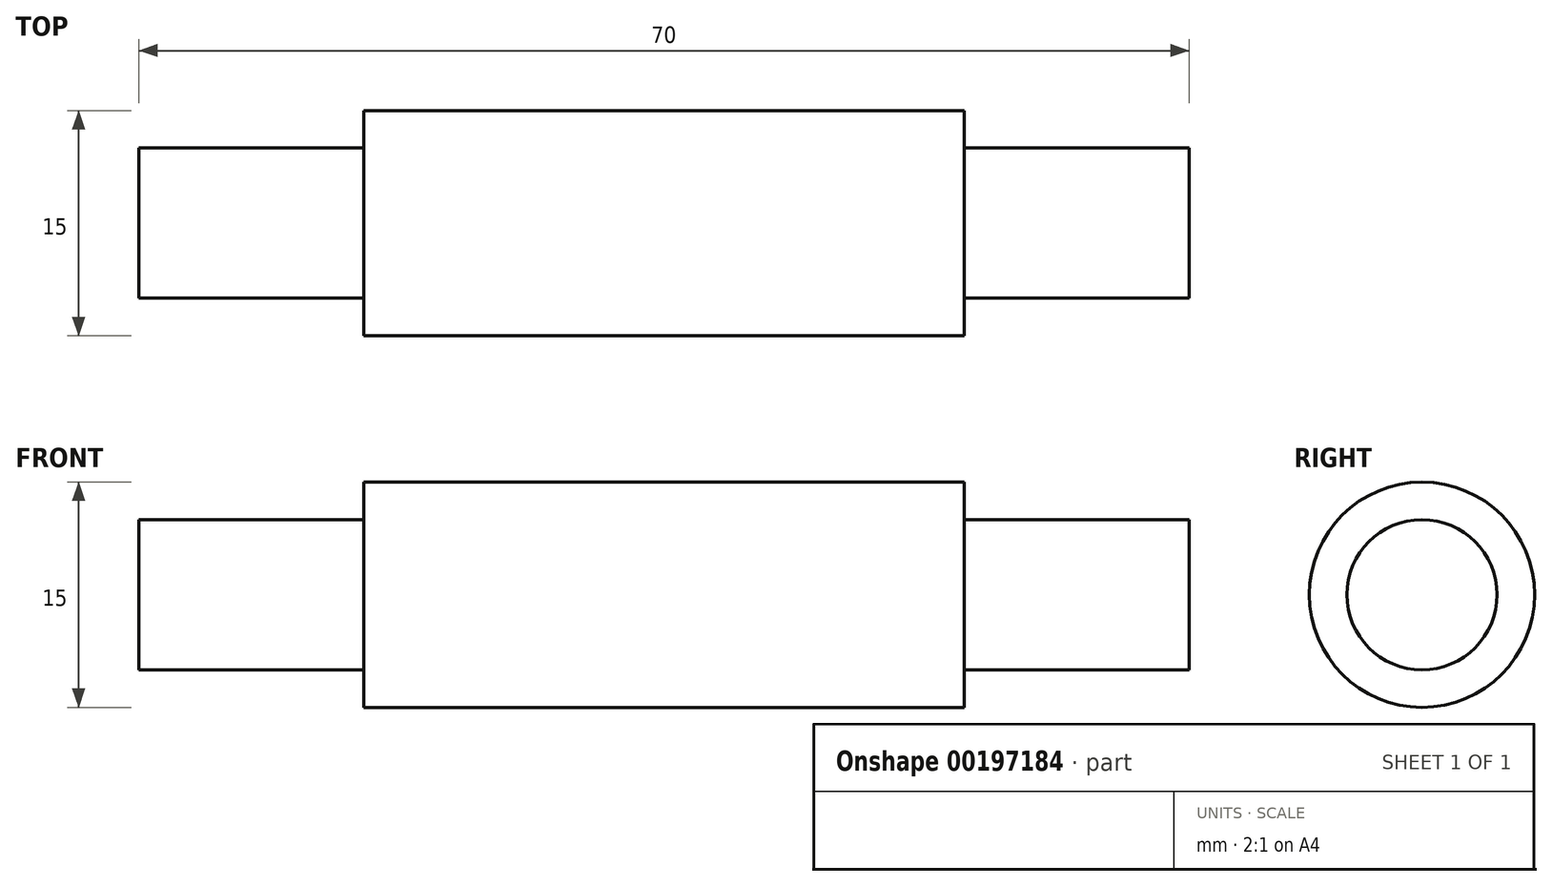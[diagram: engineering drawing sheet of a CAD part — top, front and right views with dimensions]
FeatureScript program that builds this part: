
annotation { "Feature Type Name" : "Feature", "Feature Type Description" : "" }
export const myFeature = defineFeature(function(context is Context, id is Id, definition is map)
    precondition{}
    {
        {
            var Q0;
            Q0=qCreatedBy(makeId("Right.planeOp"),FACE);
            var sketch = newSketch(context, id + "F0", { "sketchPlane" : qUnion([Q0])});
            skCircle(sketch, "E0", {"center": v(0, 0) * mm, "radius": 7.5 * mm});
            skSolve(sketch);
        }
        {
            var Q0;
            Q0 = qSketchRegion(id + "F0", true);
            extrude(context, id + "F1", {"entities" : qUnion([Q0]), "endBound" : BoundingType.SYMMETRIC, "oppositeDirection" : true, "depth" : 40 * mm});
        }
        {
            var Q0;
            Q0=makeQuery(id+"F1.opExtrude","CAP_FACE",FACE,{"disambiguationData":[OSD([sQuery(id+"F0.wireOp",EDGE,"E0")])],"isStart":true});
            var sketch = newSketch(context, id + "F2", { "sketchPlane" : qUnion([Q0])});
            skCircle(sketch, "E1", {"center": v(0, 0) * mm, "radius": 5 * mm});
            skSolve(sketch);
        }
        {
            var Q0;
            Q0 = qSketchRegion(id + "F2", true);
            extrude(context, id + "F3", {"entities" : qUnion([Q0]), "operationType" : NewBodyOperationType.ADD, "depth" : 15 * mm});
        }
        {
            var Q0;
            Q0=makeQuery(id+"F1.opExtrude","SWEPT_BODY",BODY,{"disambiguationData":[OSD([sQuery(id+"F0.wireOp",EDGE,"E0")])]});
            var Q1;
            Q1=qCreatedBy(makeId("Right.planeOp"),FACE);
            mirror(context, id + "F4", {"operationType" : NewBodyOperationType.ADD, "entities" : qUnion([Q0]), "mirrorPlane" : qUnion([Q1])});
        }
    });
